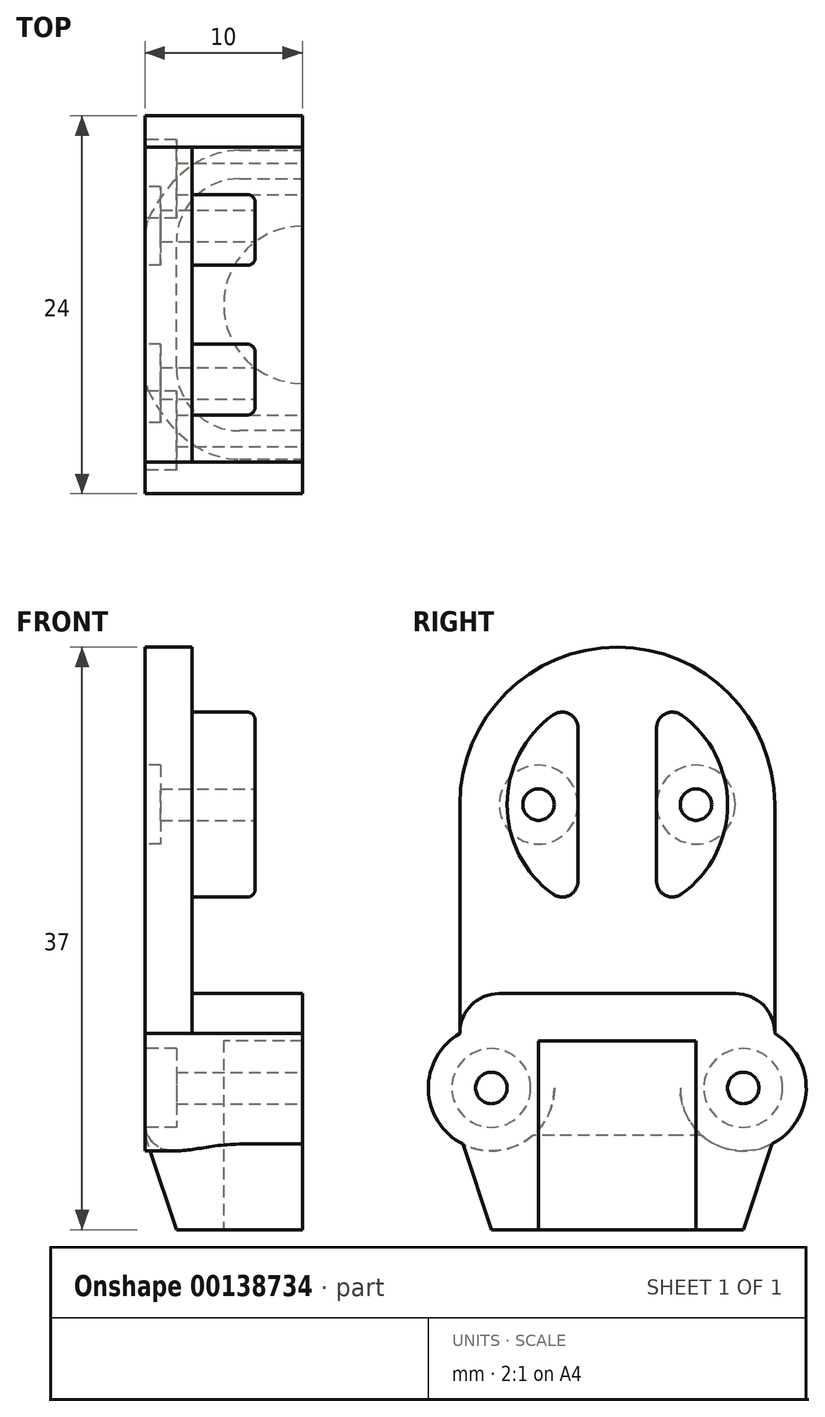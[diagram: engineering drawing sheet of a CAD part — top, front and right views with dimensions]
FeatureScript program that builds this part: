
annotation { "Feature Type Name" : "Feature", "Feature Type Description" : "" }
export const myFeature = defineFeature(function(context is Context, id is Id, definition is map)
    precondition{}
    {
        {
            var Q0;
            Q0=qCreatedBy(makeId("Right.planeOp"),FACE);
            var sketch = newSketch(context, id + "F0", { "sketchPlane" : qUnion([Q0])});
            skArc(sketch, "E0", {"start": v(-4.08, 5.69) * mm, "mid": v(-7, 0) * mm, "end": v(-4.08, -5.69) * mm});
            skCircle(sketch, "E1", {"center": v(0, 0) * mm, "radius": 2.5 * mm});
            skLineSegment(sketch, "E2", {"start": v(-2.5, 0) * mm, "end": v(-2.5, 4.87) * mm});
            skLineSegment(sketch, "E3", {"start": v(-2.5, 0) * mm, "end": v(-2.5, -4.87) * mm});
            skLineSegment(sketch, "E4", {"start": v(2.5, 0) * mm, "end": v(2.5, 4.87) * mm});
            skLineSegment(sketch, "E5", {"start": v(2.5, 0) * mm, "end": v(2.5, -4.87) * mm});
            skArc(sketch, "E6", {"start": v(-4.08, -5.69) * mm, "mid": v(-3.04, -5.76) * mm, "end": v(-2.5, -4.87) * mm});
            skArc(sketch, "E7", {"start": v(2.5, -4.87) * mm, "mid": v(3.04, -5.76) * mm, "end": v(4.08, -5.69) * mm});
            skArc(sketch, "E8", {"start": v(4.08, 5.69) * mm, "mid": v(3.04, 5.76) * mm, "end": v(2.5, 4.87) * mm});
            skArc(sketch, "E9", {"start": v(-2.5, 4.87) * mm, "mid": v(-3.04, 5.76) * mm, "end": v(-4.08, 5.69) * mm});
            skCircle(sketch, "E10", {"center": v(-5, 0) * mm, "radius": 1 * mm});
            skCircle(sketch, "E11", {"center": v(5, 0) * mm, "radius": 1 * mm});
            skArc(sketch, "E12.trimOffspring", {"start": v(4.08, -5.69) * mm, "mid": v(7, 0) * mm, "end": v(4.08, 5.69) * mm});
            skCircle(sketch, "E13", {"center": v(-8, -18) * mm, "radius": 1 * mm});
            skCircle(sketch, "E14", {"center": v(8, -18) * mm, "radius": 1 * mm});
            skSolve(sketch);
        }
        {
            var Q0;
            Q0=qCreatedBy(makeId("Front.planeOp"),FACE);
            var sketch = newSketch(context, id + "F1", { "sketchPlane" : qUnion([Q0])});
            skLineSegment(sketch, "E15.top", {"start": v(-7, -12) * mm, "end": v(0, -12) * mm});
            skLineSegment(sketch, "E15.left", {"start": v(-7, 10) * mm, "end": v(-7, -12) * mm});
            skLineSegment(sketch, "E16", {"start": v(-7, 10) * mm, "end": v(-10, 10) * mm});
            skLineSegment(sketch, "E17", {"start": v(-10, 10) * mm, "end": v(-10, -27) * mm});
            skLineSegment(sketch, "E18", {"start": v(-10, -27) * mm, "end": v(0, -27) * mm});
            skLineSegment(sketch, "E19", {"start": v(0, -27) * mm, "end": v(0, -12) * mm});
            skSolve(sketch);
        }
        {
            var Q0;
            Q0=makeQuery(id+"F0.imprint","IMPRINT",FACE,{"disambiguationData":[TD([[makeQuery(id+"F0.imprint","IMPRINT",EDGE,{"derivedFrom":sQuery(id+"F0.wireOp",EDGE,"E0")}),1.0]])]});
            var Q1;
            Q1=makeQuery(id+"F0.imprint","IMPRINT",FACE,{"disambiguationData":[TD([[makeQuery(id+"F0.imprint","IMPRINT",EDGE,{"derivedFrom":sQuery(id+"F0.wireOp",EDGE,"E4")}),-1.0]])]});
            extrude(context, id + "F2", {"entities" : qUnion([Q0, Q1]), "oppositeDirection" : true, "depth" : 7 * mm});
        }
        {
            var Q0;
            Q0 = qSketchRegion(id + "F1", true);
            extrude(context, id + "F3", {"entities" : qUnion([Q0]), "operationType" : NewBodyOperationType.ADD, "depth" : 10 * mm, "hasSecondDirection" : true, "secondDirectionOppositeDirection" : true, "secondDirectionDepth" : 10 * mm});
        }
        {
            var Q0;
            Q0=qCreatedBy(makeId("Front.planeOp"),FACE);
            var sketch = newSketch(context, id + "F4", { "sketchPlane" : qUnion([Q0])});
            skLineSegment(sketch, "E20.bottom", {"start": v(-3, 7.5) * mm, "end": v(0, 7.5) * mm});
            skLineSegment(sketch, "E20.top", {"start": v(-3, -7.5) * mm, "end": v(0, -7.5) * mm});
            skLineSegment(sketch, "E20.left", {"start": v(-3, 7.5) * mm, "end": v(-3, -7.5) * mm});
            skLineSegment(sketch, "E20.right", {"start": v(0, 7.5) * mm, "end": v(0, -7.5) * mm});
            skSolve(sketch);
        }
        {
            var Q0;
            Q0 = qSketchRegion(id + "F4", true);
            extrude(context, id + "F5", {"entities" : qUnion([Q0]), "operationType" : NewBodyOperationType.REMOVE, "oppositeDirection" : true, "depth" : 10 * mm, "hasSecondDirection" : true, "secondDirectionOppositeDirection" : false, "secondDirectionDepth" : 10 * mm});
        }
        {
            var Q0;
            Q0=makeQuery(id+"F5.boolean.opBoolean","INTERSECT",EDGE,{"derivedFrom":[makeQuery(id+"F2.opExtrude","SWEPT_FACE",FACE,{"disambiguationData":[OSD([sQuery(id+"F0.wireOp",EDGE,"E0")])]}),makeQuery(id+"F5.opExtrude","SWEPT_FACE",FACE,{"disambiguationData":[OSD([sQuery(id+"F4.wireOp",EDGE,"E20.left")])]})]});
            var Q1;
            Q1=makeQuery(id+"F5.boolean.opBoolean","INTERSECT",EDGE,{"derivedFrom":[makeQuery(id+"F2.opExtrude","SWEPT_FACE",FACE,{"disambiguationData":[OSD([sQuery(id+"F0.wireOp",EDGE,"E4"),sQuery(id+"F0.wireOp",EDGE,"E5")])]}),makeQuery(id+"F5.opExtrude","SWEPT_FACE",FACE,{"disambiguationData":[OSD([sQuery(id+"F4.wireOp",EDGE,"E20.left")])]})]});
            fillet(context, id + "F6", {"entities" : qUnion([Q0, Q1]), "radius" : .5 * mm, "tangentPropagation" : true, "allowEdgeOverflow" : false});
        }
        {
            var Q0;
            Q0=makeQuery(id+"F0.imprint","IMPRINT",FACE,{"disambiguationData":[TD([[makeQuery(id+"F0.imprint","IMPRINT",EDGE,{"derivedFrom":sQuery(id+"F0.wireOp",EDGE,"E13")}),1.0]])]});
            var Q1;
            Q1=makeQuery(id+"F0.imprint","IMPRINT",FACE,{"disambiguationData":[TD([[makeQuery(id+"F0.imprint","IMPRINT",EDGE,{"derivedFrom":sQuery(id+"F0.wireOp",EDGE,"E14")}),1.0]])]});
            extrude(context, id + "F7", {"entities" : qUnion([Q0, Q1]), "operationType" : NewBodyOperationType.REMOVE, "oppositeDirection" : true, "depth" : 25 * mm});
        }
        {
            var Q0;
            Q0=qCreatedBy(makeId("Right.planeOp"),FACE);
            var sketch = newSketch(context, id + "F8", { "sketchPlane" : qUnion([Q0])});
            skCircle(sketch, "E21", {"center": v(8, -18) * mm, "radius": 4 * mm});
            skCircle(sketch, "E22", {"center": v(-8, -18) * mm, "radius": 4 * mm});
            skCircle(sketch, "E23", {"center": v(8, -18) * mm, "radius": 2.5 * mm});
            skCircle(sketch, "E24", {"center": v(-8, -18) * mm, "radius": 2.5 * mm});
            skCircle(sketch, "E25", {"center": v(8, -18) * mm, "radius": 1 * mm});
            skCircle(sketch, "E26", {"center": v(-8, -18) * mm, "radius": 1 * mm});
            skSolve(sketch);
        }
        {
            var Q0;
            Q0 = qSketchRegion(id + "F8", true);
            var Q1;
            Q1=makeQuery(id+"F8.imprint","IMPRINT",FACE,{"disambiguationData":[TD([[makeQuery(id+"F8.imprint","IMPRINT",EDGE,{"derivedFrom":sQuery(id+"F8.wireOp",EDGE,"E23")}),1.0]])]});
            var Q2;
            Q2=makeQuery(id+"F8.imprint","IMPRINT",FACE,{"disambiguationData":[TD([[makeQuery(id+"F8.imprint","IMPRINT",EDGE,{"derivedFrom":sQuery(id+"F8.wireOp",EDGE,"E24")}),1.0]])]});
            extrude(context, id + "F9", {"entities" : qUnion([Q0, Q1, Q2]), "operationType" : NewBodyOperationType.ADD, "oppositeDirection" : true, "depth" : 10 * mm});
        }
        {
            var Q0;
            Q0=makeQuery(id+"F3.opExtrude","SWEPT_FACE",FACE,{"disambiguationData":[OSD([sQuery(id+"F1.wireOp",EDGE,"E18")])]});
            var sketch = newSketch(context, id + "F10", { "sketchPlane" : qUnion([Q0])});
            skCircle(sketch, "E27", {"center": v(0, 0) * mm, "radius": 5 * mm});
            skSolve(sketch);
        }
        {
            var Q0;
            {var subQ0=sQuery(id+"F10.wireOp",EDGE,"E27");var subQ1=makeQuery(id+"F3.opExtrude","SWEPT_EDGE",EDGE,{"disambiguationData":[OSD([sQuery(id+"F1.wireOp",EDGE,"E18"),sQuery(id+"F1.wireOp",EDGE,"E19")])]});var subQ2=makeQuery(id+"F10.imprint","INTERSECT",VERTEX,{"disambiguationData":[OD(0.0)],"derivedFrom":[subQ1,subQ0]});Q0=makeQuery(id+"F10.imprint","IMPRINT",FACE,{"disambiguationData":[TD([[makeQuery(id+"F10.imprint","IMPRINT",EDGE,{"disambiguationData":[TD([[subQ2,1.0]])],"derivedFrom":subQ0}),1.0]])]});}
            extrude(context, id + "F11", {"entities" : qUnion([Q0]), "operationType" : NewBodyOperationType.REMOVE, "oppositeDirection" : true, "depth" : 12 * mm});
        }
        {
            var Q0;
            Q0=makeQuery(id+"F9.opExtrude","CAP_FACE",FACE,{"disambiguationData":[OSD([sQuery(id+"F8.wireOp",EDGE,"E21"),sQuery(id+"F8.wireOp",EDGE,"E25")])],"isStart":false});
            var sketch = newSketch(context, id + "F12", { "sketchPlane" : qUnion([Q0])});
            skCircle(sketch, "E28", {"center": v(-8, -18) * mm, "radius": 2.5 * mm});
            skCircle(sketch, "E29", {"center": v(8, -18) * mm, "radius": 2.5 * mm});
            skSolve(sketch);
        }
        {
            var Q0;
            Q0 = qSketchRegion(id + "F12", true);
            extrude(context, id + "F13", {"entities" : qUnion([Q0]), "operationType" : NewBodyOperationType.REMOVE, "oppositeDirection" : true, "depth" : 2 * mm});
        }
        {
            var Q0;
            Q0=makeQuery(id+"F0.imprint","IMPRINT",FACE,{"disambiguationData":[TD([[makeQuery(id+"F0.imprint","IMPRINT",EDGE,{"derivedFrom":sQuery(id+"F0.wireOp",EDGE,"E10")}),1.0]])]});
            var Q1;
            Q1=makeQuery(id+"F0.imprint","IMPRINT",FACE,{"disambiguationData":[TD([[makeQuery(id+"F0.imprint","IMPRINT",EDGE,{"derivedFrom":sQuery(id+"F0.wireOp",EDGE,"E11")}),1.0]])]});
            extrude(context, id + "F14", {"entities" : qUnion([Q0, Q1]), "operationType" : NewBodyOperationType.REMOVE, "oppositeDirection" : true, "depth" : 25 * mm});
        }
        {
            var Q0;
            {var subQ0=sQuery(id+"F1.wireOp",EDGE,"E18");var subQ1=sQuery(id+"F1.wireOp",EDGE,"E17");Q0=makeQuery(id+"F9.boolean.opBoolean","SPLIT",EDGE,{"disambiguationData":[TD([makeQuery(id+"F3.opExtrude","SWEPT_FACE",FACE,{"disambiguationData":[OSD([subQ0])]})])],"derivedFrom":makeQuery(id+"F3.opExtrude","CAP_EDGE",EDGE,{"disambiguationData":[OSD([subQ1])],"isStart":true})});}
            var Q1;
            {var subQ0=sQuery(id+"F1.wireOp",EDGE,"E18");var subQ1=sQuery(id+"F1.wireOp",EDGE,"E17");Q1=makeQuery(id+"F9.boolean.opBoolean","SPLIT",EDGE,{"disambiguationData":[TD([makeQuery(id+"F3.opExtrude","SWEPT_FACE",FACE,{"disambiguationData":[OSD([subQ0])]})])],"derivedFrom":makeQuery(id+"F3.opExtrude","CAP_EDGE",EDGE,{"disambiguationData":[OSD([subQ1])],"isStart":false})});}
            fillet(context, id + "F15", {"entities" : qUnion([Q0, Q1]), "radius" : 6 * mm, "tangentPropagation" : true, "allowEdgeOverflow" : false});
        }
        {
            var Q0;
            {var subQ0=sQuery(id+"F1.wireOp",EDGE,"E18");var subQ1=makeQuery(id+"F3.opExtrude","SWEPT_FACE",FACE,{"disambiguationData":[OSD([subQ0])]});var subQ2=sQuery(id+"F1.wireOp",EDGE,"E17");Q0=makeQuery(id+"F15.opFillet","BLEND_EDGE",EDGE,{"blendedFrom":[makeQuery(id+"F9.boolean.opBoolean","SPLIT",EDGE,{"disambiguationData":[TD([subQ1])],"derivedFrom":makeQuery(id+"F3.opExtrude","CAP_EDGE",EDGE,{"disambiguationData":[OSD([subQ2])],"isStart":true})}),subQ1],"blendedInto":[subQ1]});}
            chamfer(context, id + "F16", {"entities" : qUnion([Q0]), "chamferType" : ChamferType.TWO_OFFSETS, "width1" : 2 * mm, "oppositeDirection" : false, "width2" : 6 * mm, "tangentPropagation" : true});
        }
        {
            var Q0;
            Q0=makeQuery(id+"F3.opExtrude","CAP_EDGE",EDGE,{"disambiguationData":[OSD([sQuery(id+"F1.wireOp",EDGE,"E16")])],"isStart":false});
            var Q1;
            Q1=makeQuery(id+"F3.opExtrude","CAP_EDGE",EDGE,{"disambiguationData":[OSD([sQuery(id+"F1.wireOp",EDGE,"E16")])],"isStart":true});
            fillet(context, id + "F17", {"entities" : qUnion([Q0, Q1]), "radius" : 10 * mm, "tangentPropagation" : true, "allowEdgeOverflow" : false});
        }
        {
            var Q0;
            Q0=makeQuery(id+"F3.opExtrude","SWEPT_FACE",FACE,{"disambiguationData":[OSD([sQuery(id+"F1.wireOp",EDGE,"E17")])]});
            var sketch = newSketch(context, id + "F18", { "sketchPlane" : qUnion([Q0])});
            skCircle(sketch, "E30", {"center": v(-5, 0) * mm, "radius": 2.5 * mm});
            skCircle(sketch, "E31", {"center": v(5, 0) * mm, "radius": 2.5 * mm});
            skSolve(sketch);
        }
        {
            var Q0;
            Q0=makeQuery(id+"F18.imprint","IMPRINT",FACE,{"disambiguationData":[TD([[makeQuery(id+"F18.imprint","IMPRINT",EDGE,{"derivedFrom":sQuery(id+"F18.wireOp",EDGE,"E30")}),1.0]])]});
            var Q1;
            Q1=makeQuery(id+"F18.imprint","IMPRINT",FACE,{"disambiguationData":[TD([[makeQuery(id+"F18.imprint","IMPRINT",EDGE,{"derivedFrom":sQuery(id+"F18.wireOp",EDGE,"E31")}),1.0]])]});
            extrude(context, id + "F19", {"entities" : qUnion([Q0, Q1]), "operationType" : NewBodyOperationType.REMOVE, "oppositeDirection" : true, "depth" : 1 * mm});
        }
        {
            var Q0;
            Q0=makeQuery(id+"F3.opExtrude","CAP_EDGE",EDGE,{"disambiguationData":[OSD([sQuery(id+"F1.wireOp",EDGE,"E15.top")])],"isStart":true});
            var Q1;
            Q1=makeQuery(id+"F3.opExtrude","CAP_EDGE",EDGE,{"disambiguationData":[OSD([sQuery(id+"F1.wireOp",EDGE,"E15.top")])],"isStart":false});
            fillet(context, id + "F20", {"entities" : qUnion([Q0, Q1]), "radius" : 2.5 * mm, "tangentPropagation" : true, "allowEdgeOverflow" : false});
        }
    });
